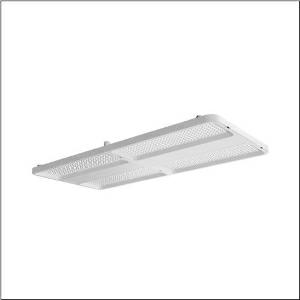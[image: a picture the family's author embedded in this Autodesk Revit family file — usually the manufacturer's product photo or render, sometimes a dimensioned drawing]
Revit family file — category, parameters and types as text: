
# Revit family: highbay_21_maxi_52hn12db4rda
name_source: partatom
category: Lighting Fixtures
units: mm (PartAtom-declared; Revit-internal decimal feet)

## family parameters
Cut with Voids When Loaded = No
Host = Face
Light Source = No
Part Type = Normal
Room Calculation Point = No
Round Connector Dimension = Use Diameter
Shared = No

## types (1)
- --- (1 x LED, 7000 lm, 38.3 W, 4000K)
    Apparent Load = 38 VA
    CIE Flux Codes = 90 98 100 100 100
    Color Rendering = 80
    Color Temperature = 4000K
    Default Elevation = 1800 mm
    Description = high bay luminaire Highbay 21 maxi; direct symmetric wide distribution, light control with lens of PMMA; UGR ≤ 22 (X = 4H | Y = 8H | S = 0.25H | reflection values 70/50/20); luminous flux: 45.000lm; light colour: 840, colour temperature: 4000K, MacAdam ≤ 3 SDCM (initial), colour rendering: CRI > 80; luminous efficacy: 188lm/W; rated service life: 75.000h (L80) at AT= ta max; control: DALI 2; luminaire connection: terminal, 5-pole, max. 2.5mm² (cable entry for one cable, Ø 8.5..16mm); mains connection: 230..240V, AC/DC 0/50..60Hz; connected load: 239,3W; protection rating (complete): IP66; insulation class (complete): insulation class I (protective earthing); protection symbol: D; impact resistance: IK08; certification: CE, ENEC, VDE, UKCA; luminaire for central battery installations according to EN 60598-2-22, internal wiring halogen-free; luminaire LABS conformity tested according to VDMA 24364:2018-05; Suitable for use in the food industry according to the specifications of IFS-Food, HACCP and/or BRC; housing frame of high-performance plastic PA6, matt traffic white (RAL 9016); cover of PMMA; dimension (LxWxH): 946 x 442 x 72mm; permissible operating ambient temperature: -40..+55°C (reducing of maximum allowable ambient temperature of 5°C with ceiling mounting); packaging unit: 1 piece; (delivery without accessories; please order mounting accessories separately)
    Height = 72 mm  [stored 0.23622 ft]
    Lamp = 1 x LED
    Lamp Light Flux = 7000 lm
    Lamp Power = 38.3 W
    Lamp count = 1
    Length = 946 mm
    Luminous efficacy = 183 lm/W
    Manufacturer = Siteco
    ModVariant = No
    Model = 52HN12DB4RDA
    Mounting Place = Ceiling
    Mounting Type = Pendant
    Number of Poles = 1
    OnlyDefault = Yes
    Power Factor = 1
    Product Name = Highbay 21 maxi
    Product group = high bay luminaire
    ProductGroupID = 902
    Protection Class = Protection class I
    Protection Degree = IP 66
    RLX_Detail_Level = 1
    RLX_Emergency_Light_Flux = 0 lm
    RLX_Emergency_Type = 0
    RLX_Emergency_Type_DB = No
    RlxData = <blob elided: 128073 chars, md5=c6c1cc32>
    Socket = socket
    Standby Power = 0 W
    System Light Flux = 7000 lm
    System Power = 38 W
    Type Comments = : DC mode (central or group accumulator) initial emergency light level
    Type Image = l_1363244.jpg
    URL = http://relux.com
    VarID = @adj_017711
    Voltage = 0 V
    Weight = 0.00 kg
    Width = 442 mm

note: [stored X ft] marks values corroborated as IEEE doubles in the binary element streams (Revit-internal decimal feet)

## geometry (parser evidence)
native form markers: Blend x4, Sweep x10
no freeform markers — native parametric forms only
